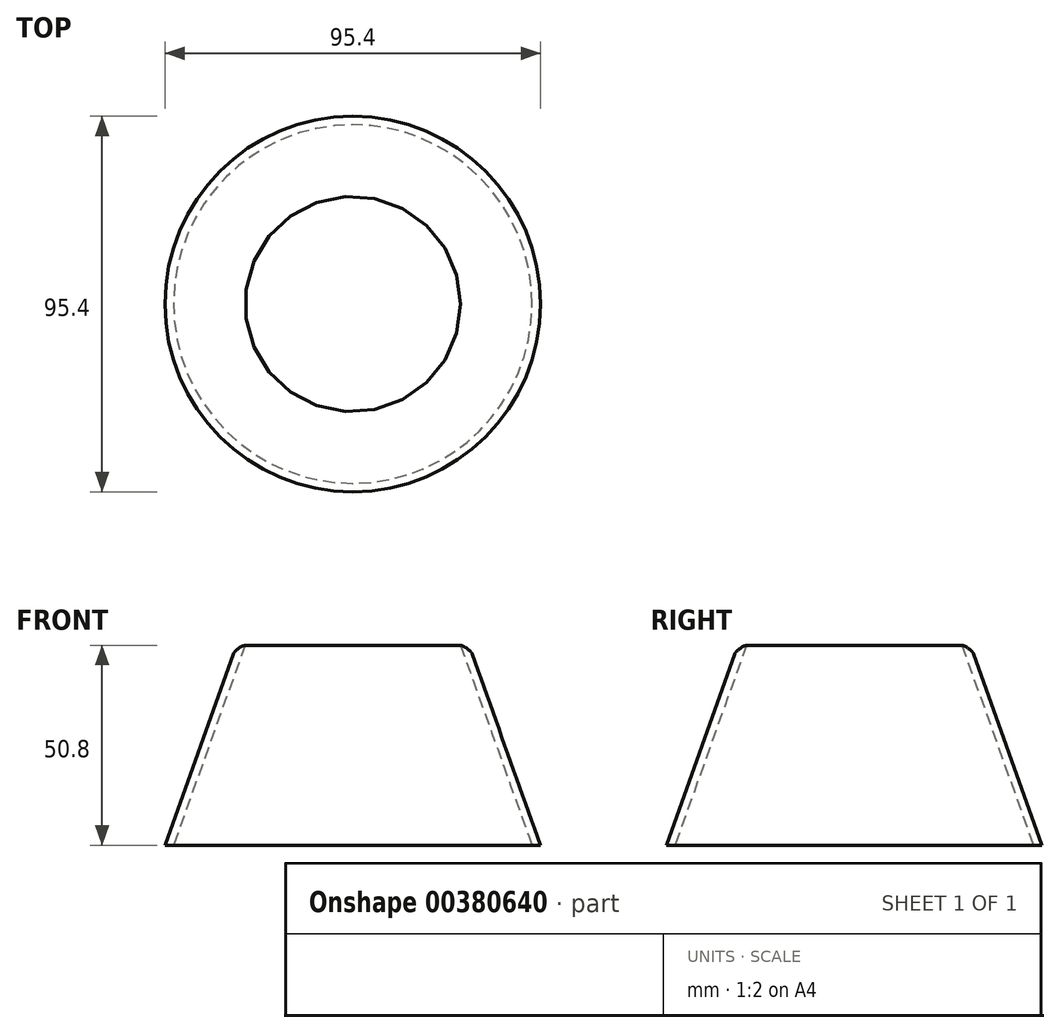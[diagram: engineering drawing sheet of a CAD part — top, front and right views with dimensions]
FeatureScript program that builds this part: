
annotation { "Feature Type Name" : "Feature", "Feature Type Description" : "" }
export const myFeature = defineFeature(function(context is Context, id is Id, definition is map)
    precondition{}
    {
        {
            var Q0;
            Q0=qCreatedBy(makeId("Top.planeOp"),FACE);
            var sketch = newSketch(context, id + "F0", { "sketchPlane" : qUnion([Q0])});
            skCircle(sketch, "E0", {"center": v(0, 0) * mm, "radius": 45.54 * mm});
            skSolve(sketch);
        }
        {
            var Q0;
            Q0=qCreatedBy(makeId("Top.planeOp"),FACE);
            var sketch = newSketch(context, id + "F1", { "sketchPlane" : qUnion([Q0])});
            skCircle(sketch, "E1", {"center": v(0, 0) * mm, "radius": 27.36 * mm});
            skSolve(sketch);
        }
        {
            var Q0;
            Q0=makeQuery(id+"F1.imprint","IMPRINT",FACE,{"disambiguationData":[TD([[makeQuery(id+"F1.imprint","IMPRINT",EDGE,{"derivedFrom":sQuery(id+"F1.wireOp",EDGE,"E1")}),1.0]])]});
            extrude(context, id + "F2", {"entities" : qUnion([Q0]), "depth" : 50.8 * mm});
        }
        {
            var Q1;
            Q1=makeQuery(id+"F0.imprint","IMPRINT",FACE,{"disambiguationData":[TD([[makeQuery(id+"F0.imprint","IMPRINT",EDGE,{"derivedFrom":sQuery(id+"F0.wireOp",EDGE,"E0")}),1.0]])]});
            var Q2;
            Q2=makeQuery(id+"F2.opExtrude","CAP_FACE",FACE,{"disambiguationData":[OSD([sQuery(id+"F1.wireOp",EDGE,"E1")])],"isStart":false});
            loft(context, id + "F3", {"operationType" : NewBodyOperationType.ADD, "sheetProfilesArray" : [{ "sheetProfileEntities" : qUnion([Q1]) }, { "sheetProfileEntities" : qUnion([Q2]) }]});
        }
        {
            var Q0;
            Q0=makeQuery(id+"F3.boolean.opBoolean","MERGE",FACE,{"derivedFrom":[makeQuery(id+"F2.opExtrude","CAP_FACE",FACE,{"disambiguationData":[OSD([sQuery(id+"F1.wireOp",EDGE,"E1")])],"isStart":true}),makeQuery(id+"F3.opLoft","CAP_FACE",FACE,{"disambiguationData":[OSD([makeQuery(id+"F0.imprint","IMPRINT",FACE,{"disambiguationData":[TD([[makeQuery(id+"F0.imprint","IMPRINT",EDGE,{"derivedFrom":sQuery(id+"F0.wireOp",EDGE,"E0")}),1.0]])]})])],"isStart":true})]});
            var Q1;
            Q1=makeQuery(id+"F2.opExtrude","CAP_FACE",FACE,{"disambiguationData":[OSD([sQuery(id+"F1.wireOp",EDGE,"E1")])],"isStart":false});
            shell(context, id + "F4", {"entities" : qUnion([Q0, Q1]), "thickness" : 2.03 * mm, "oppositeDirection" : true});
        }
        {
            var Q0;
            {var subQ0=sQuery(id+"F1.wireOp",EDGE,"E1");Q0=makeQuery(id+"F3.boolean.opBoolean","MERGE",EDGE,{"derivedFrom":[makeQuery(id+"F2.opExtrude","CAP_EDGE",EDGE,{"disambiguationData":[OSD([subQ0])],"isStart":false}),makeQuery(id+"F3.opLoft","MID_CAP_EDGE",EDGE,{"disambiguationData":[OSD([sQuery(id+"F0.wireOp",EDGE,"E0"),subQ0])],"capPos":1.0})]});}
            fillet(context, id + "F5", {"entities" : qUnion([Q0]), "radius" : 3.17 * mm, "rho" : 0.25, "crossSection" : FilletCrossSection.CONIC, "allowEdgeOverflow" : false});
        }
    });
